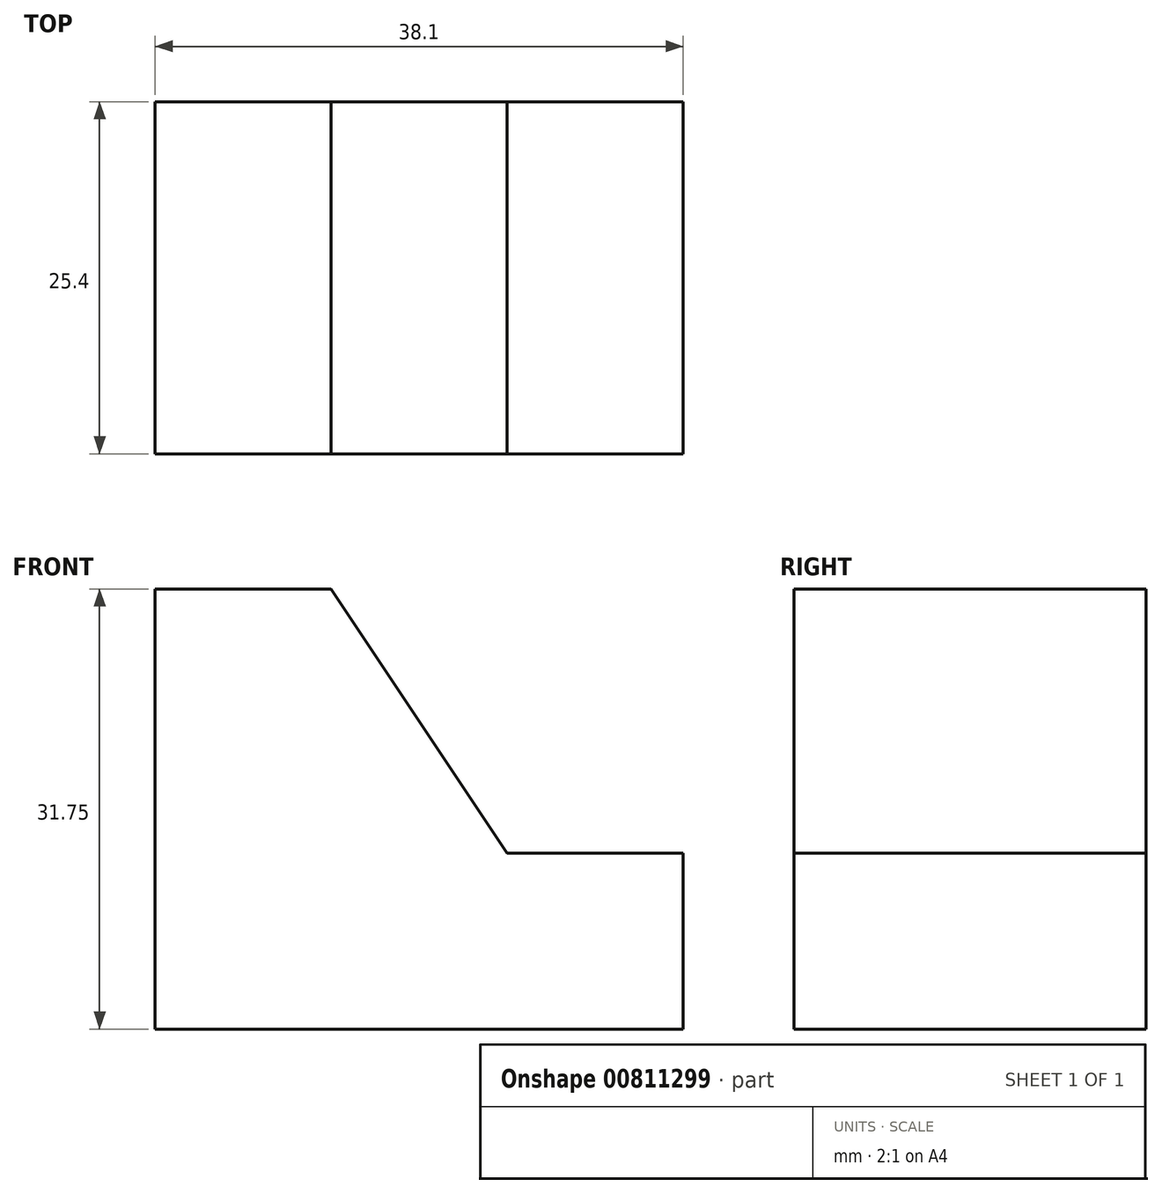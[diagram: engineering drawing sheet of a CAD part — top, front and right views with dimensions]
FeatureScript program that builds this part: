
annotation { "Feature Type Name" : "Feature", "Feature Type Description" : "" }
export const myFeature = defineFeature(function(context is Context, id is Id, definition is map)
    precondition{}
    {
        {
            var Q0;
            Q0=qCreatedBy(makeId("Front.planeOp"),FACE);
            var sketch = newSketch(context, id + "F0", { "sketchPlane" : qUnion([Q0])});
            skLineSegment(sketch, "E0", {"start": v(0, 0) * mm, "end": v(-38.1, 0) * mm});
            skLineSegment(sketch, "E1", {"start": v(-38.1, 0) * mm, "end": v(-38.1, 31.75) * mm});
            skLineSegment(sketch, "E2", {"start": v(-38.1, 31.75) * mm, "end": v(-25.4, 31.75) * mm});
            skLineSegment(sketch, "E3", {"start": v(0, 0) * mm, "end": v(0, 12.7) * mm});
            skLineSegment(sketch, "E4", {"start": v(0, 12.7) * mm, "end": v(-12.7, 12.7) * mm});
            skLineSegment(sketch, "E5", {"start": v(-12.7, 12.7) * mm, "end": v(-25.4, 31.75) * mm});
            skSolve(sketch);
        }
        {
            var Q0;
            Q0 = qSketchRegion(id + "F0", true);
            extrude(context, id + "F1", {"entities" : qUnion([Q0]), "depth" : 25.4 * mm, "offsetDistance" : 25.4 * mm});
        }
    });
